# Revit family: R17-IVLB-Generic-Downlighter Square
name_source: partatom
category: Lighting Fixtures
revit_build: Autodesk Revit 2017 (Build: 20190508_0315(x64)
units: mm (PartAtom-declared; Revit-internal decimal feet)

## family parameters
Always vertical = Yes
Cut with Voids When Loaded = No
Light Source = Yes
Part Type = Normal
Room Calculation Point = No
Round Connector Dimension = Use Diameter
Shared = No
Work Plane-Based = No

## types (1)
- Square Downlighter
    Apparent Load = 0 VA
    Assembly Code = 63.0
    Color Filter = 16777215
    Dimming Lamp Color Temperature Shift = <None>
    Downlighter Height = 100 mm  [stored 0.328084 ft]
    Luminaire Material = Rubber, Silicone
    Manufacturer = SQUARE DOWNLIGHTER
    Model = SPACE RESERVATION
    Photometric Web File = spot_ideal.ies
    Square Downlighter = Yes
    Square Downlighter - Length = 150 mm  [stored 0.492126 ft]
    Square Downlighter - Ring Size = 15 mm  [stored 0.0492126 ft]
    Square Downlighter - Width = 150 mm  [stored 0.492126 ft]
    Tilt Angle = 90.00°
    URL = www.ivlibrary.com

note: [stored X ft] marks values corroborated as IEEE doubles in the binary element streams (Revit-internal decimal feet)

## geometry (parser evidence)
native form markers: Sweep x2
no freeform markers — native parametric forms only
